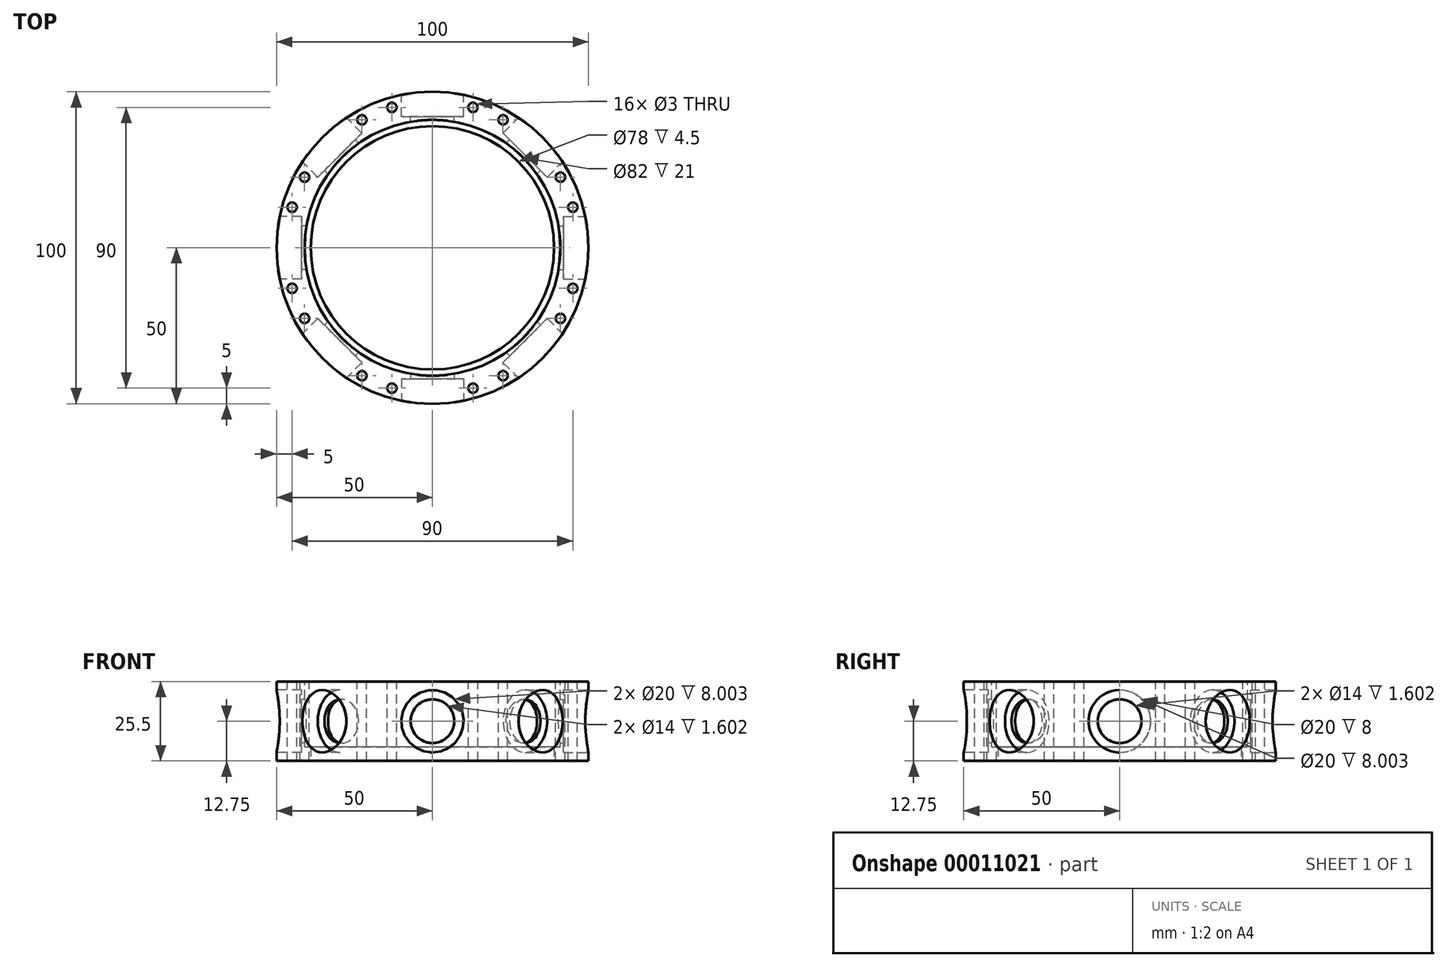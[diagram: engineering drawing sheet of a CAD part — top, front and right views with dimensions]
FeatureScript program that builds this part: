
annotation { "Feature Type Name" : "Feature", "Feature Type Description" : "" }
export const myFeature = defineFeature(function(context is Context, id is Id, definition is map)
    precondition{}
    {
        {
            var Q0;
            Q0=qCreatedBy(makeId("Top.planeOp"),FACE);
            var sketch = newSketch(context, id + "F0", { "sketchPlane" : qUnion([Q0])});
            skLineSegment(sketch, "E0.4", {"start": v(21.12, -51) * mm, "end": v(-21.12, -51) * mm});
            skArc(sketch, "E1.cCircle", {"start": v(-14.92, -36.03) * mm, "mid": v(0, -39) * mm, "end": v(14.92, -36.03) * mm});
            skLineSegment(sketch, "E2", {"start": v(-21.12, -51) * mm, "end": v(-14.92, -36.03) * mm});
            skLineSegment(sketch, "E3", {"start": v(14.92, -36.03) * mm, "end": v(21.12, -51) * mm});
            skSolve(sketch);
        }
        {
            var Q0;
            Q0=makeQuery(id+"F0.imprint","IMPRINT",FACE,{"disambiguationData":[TD([[makeQuery(id+"F0.imprint","IMPRINT",EDGE,{"derivedFrom":sQuery(id+"F0.wireOp",EDGE,"E0.4")}),-1.0]])]});
            extrude(context, id + "F1", {"entities" : qUnion([Q0]), "endBound" : BoundingType.SYMMETRIC, "depth" : 25.5 * mm});
        }
        {
            var Q0;
            Q0=makeQuery(id+"F1.opExtrude","SWEPT_FACE",FACE,{"disambiguationData":[OSD([sQuery(id+"F0.wireOp",EDGE,"E0.4")])]});
            var sketch = newSketch(context, id + "F2", { "sketchPlane" : qUnion([Q0])});
            skCircle(sketch, "E4", {"center": v(0, 0) * mm, "radius": 10 * mm});
            skSolve(sketch);
        }
        {
            var Q0;
            Q0=makeQuery(id+"F2.imprint","IMPRINT",FACE,{"disambiguationData":[TD([[makeQuery(id+"F2.imprint","IMPRINT",EDGE,{"derivedFrom":sQuery(id+"F2.wireOp",EDGE,"E4")}),1.0]])]});
            extrude(context, id + "F3", {"entities" : qUnion([Q0]), "operationType" : NewBodyOperationType.REMOVE, "oppositeDirection" : true, "depth" : 9 * mm});
        }
        {
            var Q0;
            Q0=qCreatedBy(makeId("Front.planeOp"),FACE);
            var sketch = newSketch(context, id + "F4", { "sketchPlane" : qUnion([Q0])});
            skLineSegment(sketch, "E5", {"start": v(0, 0) * mm, "end": v(0, 70.15) * mm, "construction": true});
            skSolve(sketch);
        }
        {
            var Q0;
            Q0=makeQuery(id+"F1.opExtrude","SWEPT_FACE",FACE,{"disambiguationData":[OSD([sQuery(id+"F0.wireOp",EDGE,"E0.4")])]});
            var sketch = newSketch(context, id + "F5", { "sketchPlane" : qUnion([Q0])});
            skCircle(sketch, "E6", {"center": v(0, 0) * mm, "radius": 7 * mm});
            skSolve(sketch);
        }
        {
            var Q0;
            Q0=makeQuery(id+"F5.imprint","IMPRINT",FACE,{"disambiguationData":[TD([[makeQuery(id+"F5.imprint","IMPRINT",EDGE,{"derivedFrom":sQuery(id+"F5.wireOp",EDGE,"E6")}),1.0]])]});
            var Q1;
            Q1=makeQuery(id+"F1.opExtrude","SWEPT_FACE",FACE,{"disambiguationData":[OSD([sQuery(id+"F0.wireOp",EDGE,"E1.cCircle")])]});
            extrude(context, id + "F6", {"entities" : qUnion([Q0]), "operationType" : NewBodyOperationType.REMOVE, "endBound" : BoundingType.UP_TO_SURFACE, "oppositeDirection" : true, "endBoundEntityFace" : qUnion([Q1]), "depth" : 25 * mm});
        }
        {
            var Q0;
            {var subQ0=makeQuery(id+"F1.opExtrude","CAP_FACE",FACE,{"disambiguationData":[OSD([sQuery(id+"F0.wireOp",EDGE,"E0.4"),sQuery(id+"F0.wireOp",EDGE,"E1.cCircle"),sQuery(id+"F0.wireOp",EDGE,"E2"),sQuery(id+"F0.wireOp",EDGE,"E3")])],"isStart":false});Q0=makeQuery(id+"F9.boolean.opBoolean","MERGE",FACE,{"derivedFrom":[subQ0,makeQuery(id+"F9.opPattern","COPY",FACE,{"derivedFrom":subQ0,"instanceName":"1"}),makeQuery(id+"F9.opPattern","COPY",FACE,{"derivedFrom":subQ0,"instanceName":"2"}),makeQuery(id+"F9.opPattern","COPY",FACE,{"derivedFrom":subQ0,"instanceName":"3"}),makeQuery(id+"F9.opPattern","COPY",FACE,{"derivedFrom":subQ0,"instanceName":"4"}),makeQuery(id+"F9.opPattern","COPY",FACE,{"derivedFrom":subQ0,"instanceName":"5"}),makeQuery(id+"F9.opPattern","COPY",FACE,{"derivedFrom":subQ0,"instanceName":"6"}),makeQuery(id+"F9.opPattern","COPY",FACE,{"derivedFrom":subQ0,"instanceName":"7"}),makeQuery(id+"F9.opPattern","COPY",FACE,{"derivedFrom":subQ0,"instanceName":"8"}),makeQuery(id+"F9.opPattern","COPY",FACE,{"derivedFrom":subQ0,"instanceName":"9"}),makeQuery(id+"F9.opPattern","COPY",FACE,{"derivedFrom":subQ0,"instanceName":"10"}),makeQuery(id+"F9.opPattern","COPY",FACE,{"derivedFrom":subQ0,"instanceName":"11"})]});}
            var sketch = newSketch(context, id + "F7", { "sketchPlane" : qUnion([Q0])});
            skCircle(sketch, "E7", {"center": v(-13, -45) * mm, "radius": 1.5 * mm});
            skCircle(sketch, "E8", {"center": v(13, -45) * mm, "radius": 1.5 * mm});
            skLineSegment(sketch, "E9", {"start": v(-13, -45) * mm, "end": v(13, -45) * mm, "construction": true});
            skLineSegment(sketch, "E10", {"start": v(0, 0) * mm, "end": v(0, -45) * mm, "construction": true});
            skSolve(sketch);
        }
        {
            var Q0;
            Q0 = qSketchRegion(id + "F7", true);
            extrude(context, id + "F8", {"entities" : qUnion([Q0]), "operationType" : NewBodyOperationType.REMOVE, "endBound" : BoundingType.THROUGH_ALL, "oppositeDirection" : true, "depth" : 25 * mm});
        }
        {
            var Q0;
            Q0=makeQuery(id+"F1.opExtrude","SWEPT_BODY",BODY,{"disambiguationData":[OSD([sQuery(id+"F0.wireOp",EDGE,"E0.4"),sQuery(id+"F0.wireOp",EDGE,"E1.5"),sQuery(id+"F0.wireOp",EDGE,"E2"),sQuery(id+"F0.wireOp",EDGE,"E3")])]});
            var Q1;
            Q1=sQuery(id+"F4.wireOp",EDGE,"E5");
            circularPattern(context, id + "F9", {"operationType" : NewBodyOperationType.ADD, "entities" : qUnion([Q0]), "axis" : qUnion([Q1]), "angle" : 360 * degree, "instanceCount" : 8, "equalSpace" : true});
        }
        {
            var Q0;
            {var subQ0=makeQuery(id+"F1.opExtrude","CAP_FACE",FACE,{"disambiguationData":[OSD([sQuery(id+"F0.wireOp",EDGE,"E0.4"),sQuery(id+"F0.wireOp",EDGE,"E1.5"),sQuery(id+"F0.wireOp",EDGE,"E2"),sQuery(id+"F0.wireOp",EDGE,"E3")])],"isStart":false});Q0=makeQuery(id+"F9.boolean.opBoolean","MERGE",FACE,{"derivedFrom":[subQ0,makeQuery(id+"F9.opPattern","COPY",FACE,{"derivedFrom":subQ0,"instanceName":"1"}),makeQuery(id+"F9.opPattern","COPY",FACE,{"derivedFrom":subQ0,"instanceName":"2"}),makeQuery(id+"F9.opPattern","COPY",FACE,{"derivedFrom":subQ0,"instanceName":"3"}),makeQuery(id+"F9.opPattern","COPY",FACE,{"derivedFrom":subQ0,"instanceName":"4"}),makeQuery(id+"F9.opPattern","COPY",FACE,{"derivedFrom":subQ0,"instanceName":"5"}),makeQuery(id+"F9.opPattern","COPY",FACE,{"derivedFrom":subQ0,"instanceName":"6"}),makeQuery(id+"F9.opPattern","COPY",FACE,{"derivedFrom":subQ0,"instanceName":"7"}),makeQuery(id+"F9.opPattern","COPY",FACE,{"derivedFrom":subQ0,"instanceName":"8"}),makeQuery(id+"F9.opPattern","COPY",FACE,{"derivedFrom":subQ0,"instanceName":"9"}),makeQuery(id+"F9.opPattern","COPY",FACE,{"derivedFrom":subQ0,"instanceName":"10"}),makeQuery(id+"F9.opPattern","COPY",FACE,{"derivedFrom":subQ0,"instanceName":"11"})]});}
            var sketch = newSketch(context, id + "F10", { "sketchPlane" : qUnion([Q0])});
            skCircle(sketch, "E11", {"center": v(0, 0) * mm, "radius": 41 * mm});
            skSolve(sketch);
        }
        {
            var Q0;
            Q0=makeQuery(id+"F10.imprint","IMPRINT",FACE,{"disambiguationData":[TD([[makeQuery(id+"F10.imprint","IMPRINT",EDGE,{"derivedFrom":sQuery(id+"F10.wireOp",EDGE,"E11")}),1.0]])]});
            extrude(context, id + "F11", {"entities" : qUnion([Q0]), "operationType" : NewBodyOperationType.REMOVE, "oppositeDirection" : true, "depth" : 21 * mm});
        }
        {
            var Q0;
            {var subQ0=makeQuery(id+"F1.opExtrude","CAP_FACE",FACE,{"disambiguationData":[OSD([sQuery(id+"F0.wireOp",EDGE,"E0.4"),sQuery(id+"F0.wireOp",EDGE,"E1.cCircle"),sQuery(id+"F0.wireOp",EDGE,"E2"),sQuery(id+"F0.wireOp",EDGE,"E3")])],"isStart":false});Q0=makeQuery(id+"F9.boolean.opBoolean","MERGE",FACE,{"derivedFrom":[subQ0,makeQuery(id+"F9.opPattern","COPY",FACE,{"derivedFrom":subQ0,"instanceName":"1"}),makeQuery(id+"F9.opPattern","COPY",FACE,{"derivedFrom":subQ0,"instanceName":"2"}),makeQuery(id+"F9.opPattern","COPY",FACE,{"derivedFrom":subQ0,"instanceName":"3"}),makeQuery(id+"F9.opPattern","COPY",FACE,{"derivedFrom":subQ0,"instanceName":"4"}),makeQuery(id+"F9.opPattern","COPY",FACE,{"derivedFrom":subQ0,"instanceName":"5"}),makeQuery(id+"F9.opPattern","COPY",FACE,{"derivedFrom":subQ0,"instanceName":"6"}),makeQuery(id+"F9.opPattern","COPY",FACE,{"derivedFrom":subQ0,"instanceName":"7"}),makeQuery(id+"F9.opPattern","COPY",FACE,{"derivedFrom":subQ0,"instanceName":"8"}),makeQuery(id+"F9.opPattern","COPY",FACE,{"derivedFrom":subQ0,"instanceName":"9"}),makeQuery(id+"F9.opPattern","COPY",FACE,{"derivedFrom":subQ0,"instanceName":"10"}),makeQuery(id+"F9.opPattern","COPY",FACE,{"derivedFrom":subQ0,"instanceName":"11"})]});}
            var sketch = newSketch(context, id + "F12", { "sketchPlane" : qUnion([Q0])});
            skCircle(sketch, "E12", {"center": v(0, 0) * mm, "radius": 50 * mm});
            skSolve(sketch);
        }
        {
            var Q0;
            Q0=makeQuery(id+"F12.imprint","IMPRINT",FACE,{"disambiguationData":[TD([[makeQuery(id+"F12.imprint","IMPRINT",EDGE,{"derivedFrom":sQuery(id+"F12.wireOp",EDGE,"E12")}),-1.0]])]});
            extrude(context, id + "F13", {"entities" : qUnion([Q0]), "operationType" : NewBodyOperationType.REMOVE, "endBound" : BoundingType.THROUGH_ALL, "oppositeDirection" : true, "depth" : 25 * mm});
        }
    });
